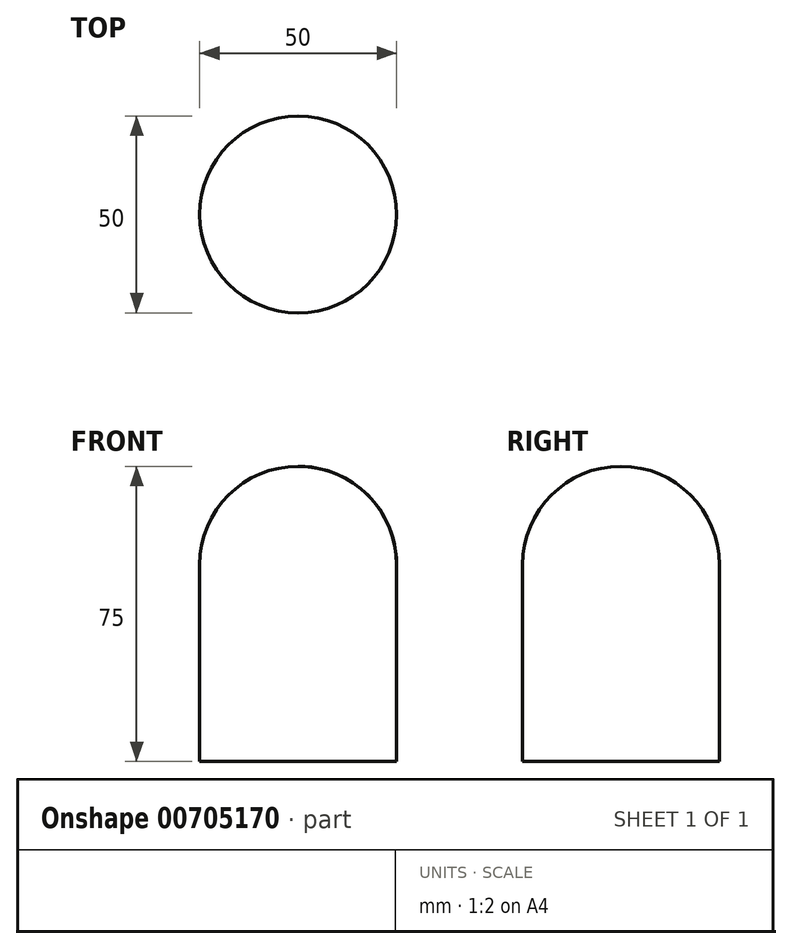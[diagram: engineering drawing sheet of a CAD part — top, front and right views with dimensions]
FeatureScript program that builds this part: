
annotation { "Feature Type Name" : "Feature", "Feature Type Description" : "" }
export const myFeature = defineFeature(function(context is Context, id is Id, definition is map)
    precondition{}
    {
        {
            var Q0;
            Q0=qCreatedBy(makeId("Front.planeOp"),FACE);
            var sketch = newSketch(context, id + "F0", { "sketchPlane" : qUnion([Q0])});
            skLineSegment(sketch, "E0", {"start": v(-25, 0) * mm, "end": v(-25, 50) * mm});
            skArc(sketch, "E1", {"start": v(-25, 50) * mm, "mid": v(-17.68, 67.68) * mm, "end": v(0, 75) * mm});
            skLineSegment(sketch, "E2", {"start": v(-25, 0) * mm, "end": v(0, 0) * mm});
            skLineSegment(sketch, "E3", {"start": v(0, 75) * mm, "end": v(0, 0) * mm});
            skSolve(sketch);
        }
        {
            var Q0;
            Q0 = qSketchRegion(id + "F0", true);
            var Q1;
            Q1=sQuery(id+"F0.wireOp",EDGE,"E3");
            revolve(context, id + "F1", {"surfaceOperationType" : NewSurfaceOperationType.NEW, "entities" : qUnion([Q0]), "axis" : qUnion([Q1]), "revolveType" : RevolveType.FULL});
        }
    });
